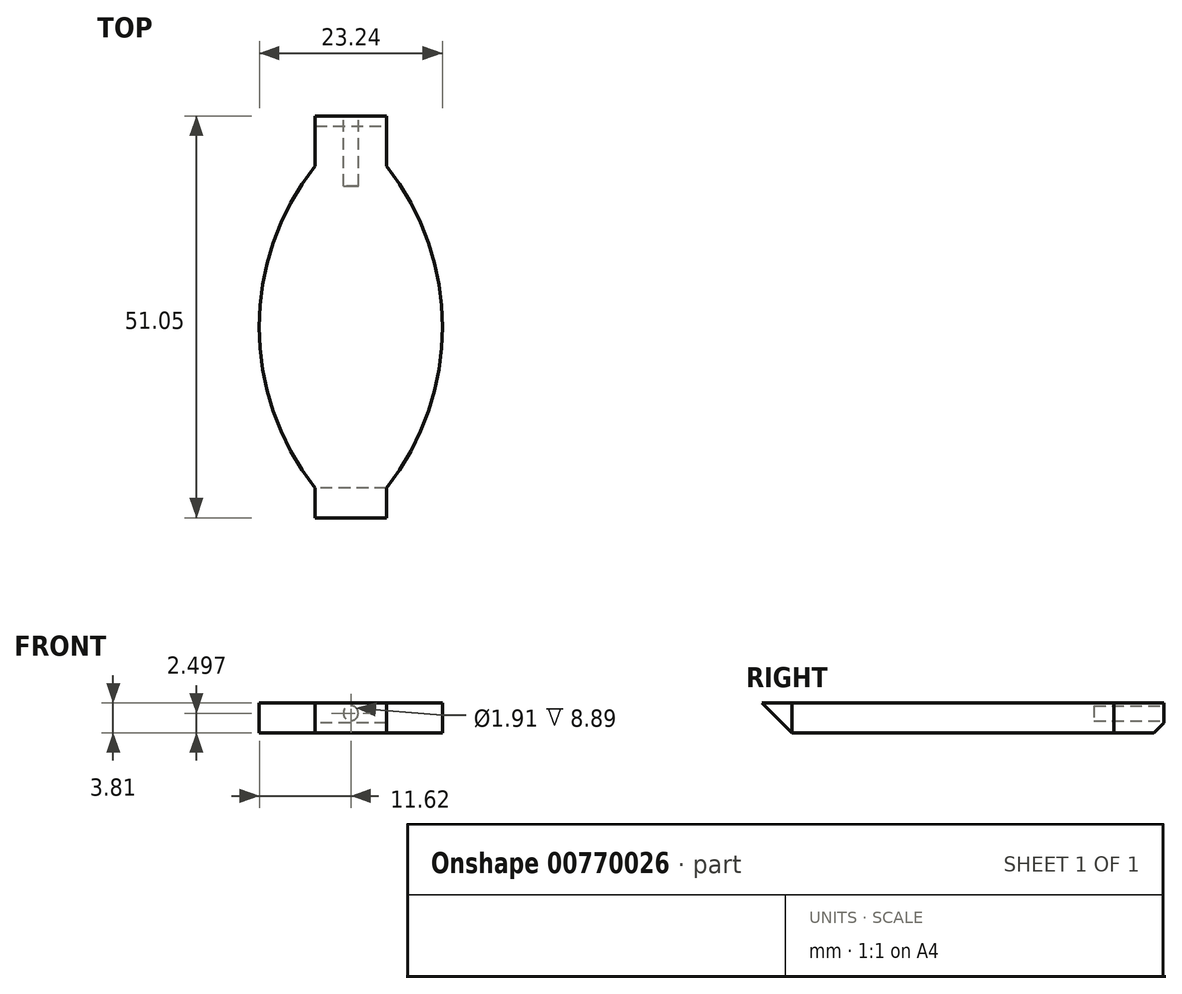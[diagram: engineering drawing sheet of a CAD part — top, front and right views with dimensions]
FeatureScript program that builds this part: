
annotation { "Feature Type Name" : "Feature", "Feature Type Description" : "" }
export const myFeature = defineFeature(function(context is Context, id is Id, definition is map)
    precondition{}
    {
        {
            var Q0;
            Q0=qCreatedBy(makeId("Top.planeOp"),FACE);
            var sketch = newSketch(context, id + "F0", { "sketchPlane" : qUnion([Q0])});
            skLineSegment(sketch, "E0.top", {"start": v(-4.53, -2.42) * mm, "end": v(4.53, -2.42) * mm});
            skPoint(sketch, "E0.middle", {"position": v(0, 0) * mm});
            skLineSegment(sketch, "E1", {"start": v(-4.53, -43.3) * mm, "end": v(4.53, -43.3) * mm});
            skArc(sketch, "E2", {"start": v(4.53, -43.3) * mm, "mid": v(11.62, -22.86) * mm, "end": v(4.53, -2.42) * mm});
            skArc(sketch, "E3", {"start": v(-4.53, -2.42) * mm, "mid": v(-11.62, -22.86) * mm, "end": v(-4.53, -43.3) * mm});
            skSolve(sketch);
        }
        {
            var Q0;
            Q0 = qSketchRegion(id + "F0", true);
            extrude(context, id + "F1", {"entities" : qUnion([Q0]), "depth" : 3.8 * mm, "offsetDistance" : 25.4 * mm});
        }
        {
            var Q0;
            Q0=makeQuery(id+"F1.opExtrude","SWEPT_FACE",FACE,{"disambiguationData":[OSD([sQuery(id+"F0.wireOp",EDGE,"E0.top")])]});
            var sketch = newSketch(context, id + "F2", { "sketchPlane" : qUnion([Q0])});
            skLineSegment(sketch, "E4.bottom", {"start": v(-4.53, 3.81) * mm, "end": v(4.53, 3.81) * mm});
            skLineSegment(sketch, "E4.top", {"start": v(-4.53, 0) * mm, "end": v(4.53, 0) * mm});
            skLineSegment(sketch, "E4.left", {"start": v(-4.53, 3.81) * mm, "end": v(-4.53, 0) * mm});
            skLineSegment(sketch, "E4.right", {"start": v(4.53, 3.81) * mm, "end": v(4.53, 0) * mm});
            skSolve(sketch);
        }
        {
            var Q0;
            Q0 = qSketchRegion(id + "F2", true);
            extrude(context, id + "F3", {"entities" : qUnion([Q0]), "operationType" : NewBodyOperationType.ADD, "depth" : 6.35 * mm, "offsetDistance" : 25.4 * mm});
        }
        {
            var Q0;
            Q0=makeQuery(id+"F3.opExtrude","CAP_EDGE",EDGE,{"disambiguationData":[OSD([sQuery(id+"F2.wireOp",EDGE,"E4.top")])],"isStart":false});
            chamfer(context, id + "F4", {"entities" : qUnion([Q0]), "width" : 1.27 * mm, "tangentPropagation" : true});
        }
        {
            var Q0;
            Q0=makeQuery(id+"F1.opExtrude","SWEPT_FACE",FACE,{"disambiguationData":[OSD([sQuery(id+"F0.wireOp",EDGE,"E1")])]});
            var sketch = newSketch(context, id + "F5", { "sketchPlane" : qUnion([Q0])});
            skLineSegment(sketch, "E5.bottom", {"start": v(-4.53, 3.81) * mm, "end": v(4.53, 3.81) * mm});
            skLineSegment(sketch, "E5.top", {"start": v(-4.53, 0) * mm, "end": v(4.53, 0) * mm});
            skLineSegment(sketch, "E5.left", {"start": v(-4.53, 3.81) * mm, "end": v(-4.53, 0) * mm});
            skLineSegment(sketch, "E5.right", {"start": v(4.53, 3.81) * mm, "end": v(4.53, 0) * mm});
            skSolve(sketch);
        }
        {
            var Q0;
            Q0 = qSketchRegion(id + "F5", true);
            extrude(context, id + "F6", {"entities" : qUnion([Q0]), "operationType" : NewBodyOperationType.ADD, "depth" : 5.08 * mm, "offsetDistance" : 25.4 * mm});
        }
        {
            var Q0;
            Q0=makeQuery(id+"F6.opExtrude","CAP_EDGE",EDGE,{"disambiguationData":[OSD([sQuery(id+"F5.wireOp",EDGE,"E5.top")])],"isStart":false});
            chamfer(context, id + "F7", {"entities" : qUnion([Q0]), "width" : 5.08 * mm, "tangentPropagation" : true});
        }
        {
            var Q0;
            Q0=makeQuery(id+"F3.opExtrude","CAP_FACE",FACE,{"disambiguationData":[OSD([sQuery(id+"F2.wireOp",EDGE,"E4.bottom"),sQuery(id+"F2.wireOp",EDGE,"E4.top"),sQuery(id+"F2.wireOp",EDGE,"E4.left"),sQuery(id+"F2.wireOp",EDGE,"E4.right")])],"isStart":false});
            var sketch = newSketch(context, id + "F8", { "sketchPlane" : qUnion([Q0])});
            skCircle(sketch, "E6", {"center": v(0, 2.5) * mm, "radius": 0.95 * mm});
            skPoint(sketch, "E6.centerSnap0", {"position": v(0, 1.27) * mm});
            skSolve(sketch);
        }
        {
            var Q0;
            Q0 = qSketchRegion(id + "F8", true);
            extrude(context, id + "F9", {"entities" : qUnion([Q0]), "operationType" : NewBodyOperationType.REMOVE, "oppositeDirection" : true, "depth" : 8.9 * mm, "offsetDistance" : 25.4 * mm});
        }
    });
